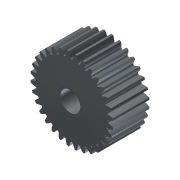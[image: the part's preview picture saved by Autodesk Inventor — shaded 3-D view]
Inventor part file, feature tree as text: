
AUTODESK INVENTOR PART (.ipt)
format: ipt  version: 2013 (Build 170138000, 138)  size: 442,880 bytes
history: native  units: in
note: dims shown in document units (in); Inventor stores cm internally (conversion verified against a paired STEP export)
features: mirror x1, other x1, imported_body x1
ambient origin geometry x8: Origin, YZ Plane, XZ Plane, XY Plane, X Axis, Y Axis, Z Axis, Center Point
feature tree (3):
  mirror  "Mirror1"
  other  "217-2625-005 Rev1_Planet_Revolving_Follower011"
  imported_body  "Base1"
